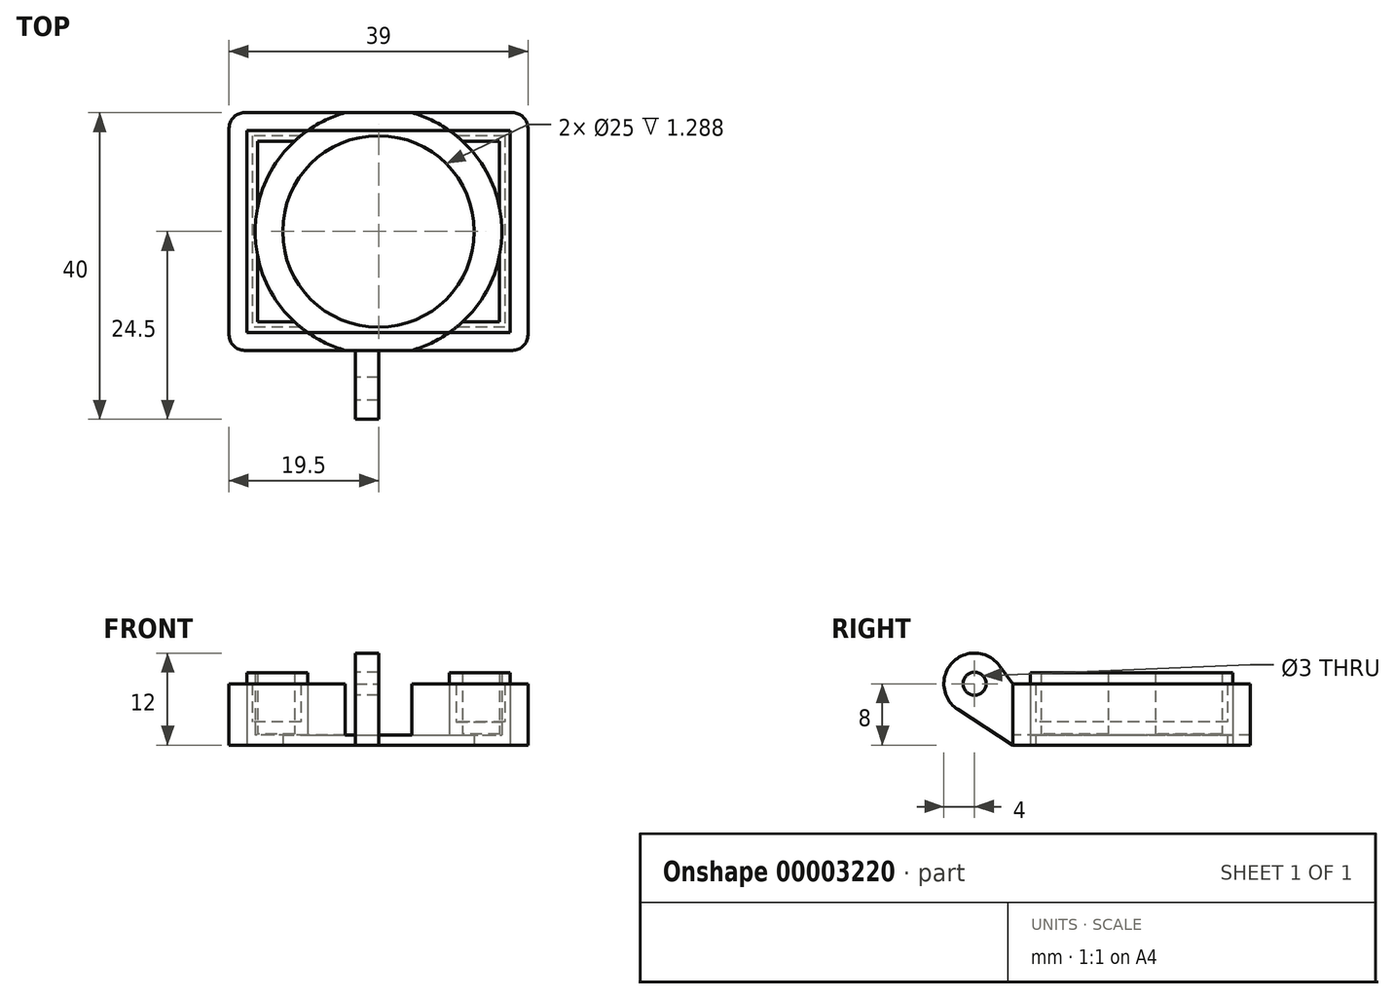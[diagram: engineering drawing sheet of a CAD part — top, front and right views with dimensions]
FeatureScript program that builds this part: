
annotation { "Feature Type Name" : "Feature", "Feature Type Description" : "" }
export const myFeature = defineFeature(function(context is Context, id is Id, definition is map)
    precondition{}
    {
        {
            var Q0;
            Q0=qCreatedBy(makeId("Top.planeOp"),FACE);
            var sketch = newSketch(context, id + "F0", { "sketchPlane" : qUnion([Q0])});
            skLineSegment(sketch, "E0.rect.bottom", {"start": v(17.5, 15.5) * mm, "end": v(-17.5, 15.5) * mm});
            skLineSegment(sketch, "E0.rect.top", {"start": v(17.5, -15.5) * mm, "end": v(-17.5, -15.5) * mm});
            skLineSegment(sketch, "E0.rect.left", {"start": v(19.5, 13.5) * mm, "end": v(19.5, -13.5) * mm});
            skLineSegment(sketch, "E0.rect.right", {"start": v(-19.5, 13.5) * mm, "end": v(-19.5, -13.5) * mm});
            skPoint(sketch, "E0.rect.middle", {"position": v(0, 0) * mm});
            skPoint(sketch, "E1.visualSharp", {"position": v(19.5, 15.5) * mm});
            skArc(sketch, "E1.filletArc", {"start": v(19.5, 13.5) * mm, "mid": v(18.91, 14.91) * mm, "end": v(17.5, 15.5) * mm});
            skPoint(sketch, "E2.visualSharp", {"position": v(19.5, -15.5) * mm});
            skArc(sketch, "E2.filletArc", {"start": v(17.5, -15.5) * mm, "mid": v(18.91, -14.91) * mm, "end": v(19.5, -13.5) * mm});
            skPoint(sketch, "E3.visualSharp", {"position": v(-19.5, -15.5) * mm});
            skArc(sketch, "E3.filletArc", {"start": v(-19.5, -13.5) * mm, "mid": v(-18.91, -14.91) * mm, "end": v(-17.5, -15.5) * mm});
            skPoint(sketch, "E4.visualSharp", {"position": v(-19.5, 15.5) * mm});
            skArc(sketch, "E4.filletArc", {"start": v(-17.5, 15.5) * mm, "mid": v(-18.91, 14.91) * mm, "end": v(-19.5, 13.5) * mm});
            skSolve(sketch);
        }
        {
            var Q0;
            Q0=makeQuery(id+"F0.imprint","IMPRINT",FACE,{"disambiguationData":[TD([[makeQuery(id+"F0.imprint","IMPRINT",EDGE,{"derivedFrom":sQuery(id+"F0.wireOp",EDGE,"E0.rect.bottom")}),1.0]])]});
            extrude(context, id + "F1", {"entities" : qUnion([Q0]), "depth" : 8 * mm});
        }
        {
            var Q0;
            Q0=qCreatedBy(makeId("Top.planeOp"),FACE);
            var sketch = newSketch(context, id + "F2", { "sketchPlane" : qUnion([Q0])});
            skLineSegment(sketch, "E5.rect.bottom", {"start": v(17.2, 13.2) * mm, "end": v(-17.2, 13.2) * mm});
            skLineSegment(sketch, "E5.rect.top", {"start": v(17.2, -13.2) * mm, "end": v(-17.2, -13.2) * mm});
            skLineSegment(sketch, "E5.rect.left", {"start": v(17.2, 13.2) * mm, "end": v(17.2, -13.2) * mm});
            skLineSegment(sketch, "E5.rect.right", {"start": v(-17.2, 13.2) * mm, "end": v(-17.2, -13.2) * mm});
            skPoint(sketch, "E5.rect.middle", {"position": v(0, 0) * mm});
            skSolve(sketch);
        }
        {
            var Q0;
            Q0=makeQuery(id+"F2.imprint","IMPRINT",FACE,{"disambiguationData":[TD([[makeQuery(id+"F2.imprint","IMPRINT",EDGE,{"derivedFrom":sQuery(id+"F2.wireOp",EDGE,"E5.rect.bottom")}),1.0]])]});
            var Q1;
            Q1=sQuery(id+"F2.wireOp",EDGE,"E5.rect.bottom");
            var Q2;
            Q2=sQuery(id+"F2.wireOp",EDGE,"E5.rect.right");
            var Q3;
            Q3=sQuery(id+"F2.wireOp",EDGE,"E5.rect.top");
            var Q4;
            Q4=sQuery(id+"F2.wireOp",EDGE,"E5.rect.left");
            extrude(context, id + "F3", {"entities" : qUnion([Q0]), "surfaceEntities" : qUnion([Q1, Q2, Q3, Q4]), "depth" : 9.4 * mm});
        }
        {
            var Q0;
            Q0=makeQuery(id+"F3.opExtrude","CAP_FACE",FACE,{"disambiguationData":[OSD([sQuery(id+"F2.wireOp",EDGE,"E5.rect.bottom"),sQuery(id+"F2.wireOp",EDGE,"E5.rect.top"),sQuery(id+"F2.wireOp",EDGE,"E5.rect.left"),sQuery(id+"F2.wireOp",EDGE,"E5.rect.right")])],"isStart":false});
            var Q1;
            Q1=makeQuery(id+"F3.opExtrude","CAP_FACE",FACE,{"disambiguationData":[OSD([sQuery(id+"F2.wireOp",EDGE,"E5.rect.bottom"),sQuery(id+"F2.wireOp",EDGE,"E5.rect.top"),sQuery(id+"F2.wireOp",EDGE,"E5.rect.left"),sQuery(id+"F2.wireOp",EDGE,"E5.rect.right")])],"isStart":false});
            shell(context, id + "F4", {"entities" : qUnion([Q0, Q1]), "thickness" : 1.4 * mm});
        }
        {
            var Q0;
            Q0=makeQuery(id+"F1.opExtrude","CAP_FACE",FACE,{"disambiguationData":[OSD([sQuery(id+"F0.wireOp",EDGE,"E0.rect.bottom"),sQuery(id+"F0.wireOp",EDGE,"E0.rect.top"),sQuery(id+"F0.wireOp",EDGE,"E0.rect.left"),sQuery(id+"F0.wireOp",EDGE,"E0.rect.right"),sQuery(id+"F0.wireOp",EDGE,"E1.filletArc"),sQuery(id+"F0.wireOp",EDGE,"E2.filletArc"),sQuery(id+"F0.wireOp",EDGE,"E3.filletArc"),sQuery(id+"F0.wireOp",EDGE,"E4.filletArc")])],"isStart":false});
            shell(context, id + "F5", {"entities" : qUnion([Q0]), "thickness" : 3 * mm});
        }
        {
            var Q0;
            Q0=qCreatedBy(makeId("Front.planeOp"),FACE);
            var sketch = newSketch(context, id + "F6", { "sketchPlane" : qUnion([Q0])});
            skLineSegment(sketch, "E6", {"start": v(0, 0) * mm, "end": v(-12.5, 0) * mm});
            skLineSegment(sketch, "E7", {"start": v(-12.5, 0) * mm, "end": v(-12.5, 1.29) * mm});
            skLineSegment(sketch, "E8", {"start": v(-12.5, 1.29) * mm, "end": v(-16.1, 1.29) * mm});
            skLineSegment(sketch, "E9", {"start": v(-16.1, 1.29) * mm, "end": v(-16.1, 13.93) * mm});
            skLineSegment(sketch, "E10", {"start": v(-16.1, 13.93) * mm, "end": v(0, 13.93) * mm});
            skLineSegment(sketch, "E11", {"start": v(0, 13.93) * mm, "end": v(0, 0) * mm});
            skSolve(sketch);
        }
        {
            var Q0;
            Q0=makeQuery(id+"F6.imprint","IMPRINT",FACE,{"disambiguationData":[TD([[makeQuery(id+"F6.imprint","IMPRINT",EDGE,{"derivedFrom":sQuery(id+"F6.wireOp",EDGE,"E6")}),-1.0]])]});
            var Q1;
            Q1=sQuery(id+"F6.wireOp",EDGE,"E11");
            revolve(context, id + "F7", {"operationType" : NewBodyOperationType.REMOVE, "entities" : qUnion([Q0]), "axis" : qUnion([Q1]), "revolveType" : RevolveType.FULL, "oppositeDirection" : true});
        }
        {
            var Q0;
            Q0=qCreatedBy(makeId("Right.planeOp"),FACE);
            var sketch = newSketch(context, id + "F8", { "sketchPlane" : qUnion([Q0])});
            skLineSegment(sketch, "E12", {"start": v(0, 0) * mm, "end": v(-15.5, 0) * mm, "construction": true});
            skLineSegment(sketch, "E13", {"start": v(-15.5, 0) * mm, "end": v(-15.5, 8) * mm});
            skLineSegment(sketch, "E14", {"start": v(-15.5, 8) * mm, "end": v(-17.3, 10.4) * mm});
            skLineSegment(sketch, "E15", {"start": v(-15.5, 8) * mm, "end": v(-20.5, 8) * mm, "construction": true});
            skArc(sketch, "E16", {"start": v(-17.3, 10.4) * mm, "mid": v(-23.42, 10.73) * mm, "end": v(-22.67, 4.64) * mm});
            skLineSegment(sketch, "E17", {"start": v(-15.5, 0) * mm, "end": v(-22.67, 4.64) * mm});
            skLineSegment(sketch, "E18", {"start": v(-15.5, 8) * mm, "end": v(-15.5, 12) * mm, "construction": true});
            skLineSegment(sketch, "E19", {"start": v(-15.5, 12) * mm, "end": v(-20.5, 12) * mm, "construction": true});
            skSolve(sketch);
        }
        {
            var Q0;
            Q0=makeQuery(id+"F8.imprint","IMPRINT",FACE,{"disambiguationData":[TD([[makeQuery(id+"F8.imprint","IMPRINT",EDGE,{"derivedFrom":sQuery(id+"F8.wireOp",EDGE,"E13")}),1.0]])]});
            extrude(context, id + "F9", {"entities" : qUnion([Q0]), "operationType" : NewBodyOperationType.ADD, "oppositeDirection" : true, "depth" : 3 * mm});
        }
        {
            var Q0;
            Q0=makeQuery(id+"F9.opExtrude","CAP_FACE",FACE,{"disambiguationData":[OSD([sQuery(id+"F8.wireOp",EDGE,"E13"),sQuery(id+"F8.wireOp",EDGE,"E14"),sQuery(id+"F8.wireOp",EDGE,"E16"),sQuery(id+"F8.wireOp",EDGE,"E17")])],"isStart":false});
            var sketch = newSketch(context, id + "F10", { "sketchPlane" : qUnion([Q0])});
            skCircle(sketch, "E20", {"center": v(20.5, 8) * mm, "radius": 1.5 * mm});
            skSolve(sketch);
        }
        {
            var Q0;
            Q0=makeQuery(id+"F10.imprint","IMPRINT",FACE,{"disambiguationData":[TD([[makeQuery(id+"F10.imprint","IMPRINT",EDGE,{"derivedFrom":sQuery(id+"F10.wireOp",EDGE,"E20")}),1.0]])]});
            extrude(context, id + "F11", {"entities" : qUnion([Q0]), "operationType" : NewBodyOperationType.REMOVE, "endBound" : BoundingType.THROUGH_ALL, "oppositeDirection" : true, "depth" : 25 * mm});
        }
    });
